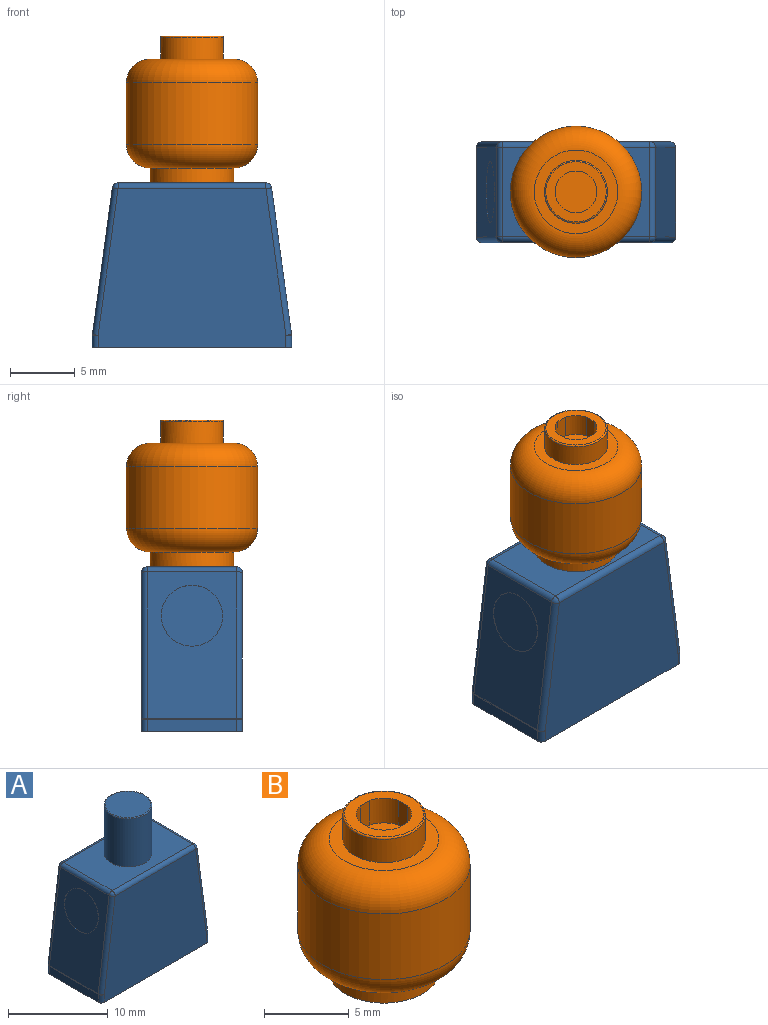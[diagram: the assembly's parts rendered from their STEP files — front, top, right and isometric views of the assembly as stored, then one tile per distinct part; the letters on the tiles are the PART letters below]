
ASSEMBLY  parts=2 mates=1
PART A: 114 faces, bbox 15.4x7.8x18.8 mm
  f0: plane 4.98x2.09mm, normal (0,0,-1), area 6.8mm2, adj f1,f4,f8,f81,f95,f112
  f1: cylinder r=1.5mm len=17.75mm, axis (0,0,-1), area 20.6mm2, adj f0,f16,f81,f82,f105,f112,f113
  f2: cylinder r=1mm len=11.88mm, axis (0,0,-1), area 12.4mm2, adj f10,f80,f87,f105
  f3: cylinder r=1mm len=11.88mm, axis (0,0,-1), area 12.4mm2, adj f11,f88,f89,f96
  f4: cylinder r=1.5mm len=17.75mm, axis (0,0,-1), area 20.6mm2, adj f0,f16,f94,f95,f96,f112,f113
  f5: plane 11.88x0.48mm, normal (0,-1,0), area 5.7mm2, adj f11,f16,f64,f88
  f6: plane 11.88x0.48mm, normal (0,1,0), area 5.7mm2, adj f11,f16,f73,f91
  f7: plane 4.98x2.09mm, normal (0,0,-1), area 6.8mm2, adj f9,f83,f84,f92,f93,f111
  f8: plane 11.88x4.98mm, normal (0,-1,0), area 59.2mm2, adj f0,f16,f81,f95
  f9: plane 11.88x4.98mm, normal (0,1,0), area 59.2mm2, adj f7,f16,f84,f92
  f10: plane 6.06x3.84mm, normal (0,0,-1), area 18.7mm2, adj f2,f13,f15,f26,f27,f29,f52,f53
  f11: plane 6.06x3.84mm, normal (0,0,-1), area 18.7mm2, adj f3,f5,f6,f12,f14,f28,f55,f56
  f12: plane 11.88x2.58mm, normal (0,-1,0), area 22.5mm2, adj f11,f16,f24,f28,f65
  f13: plane 11.88x0.48mm, normal (0,-1,0), area 5.7mm2, adj f10,f16,f69,f80
  f14: plane 11.88x2.58mm, normal (0,1,0), area 22.5mm2, adj f11,f16,f24,f28,f72
  f15: plane 11.88x0.48mm, normal (0,1,0), area 5.7mm2, adj f10,f16,f78,f85
  f16: plane 15.4x7.8mm, normal (0,0,-1), area 42.5mm2, adj f1,f4,f5,f6,f8,f9,f12,f13
  f17: plane 6.92x0.97mm, normal (1,0,0), area 6.7mm2, adj f16,f30,f32,f33
  f18: plane 6.92x0.97mm, normal (-1,0,0), area 6.7mm2, adj f16,f37,f45,f46
  f19: plane 14.52x12.31mm, normal (0,-1,0), area 161.2mm2, adj f16,f30,f34,f37,f40,f41
  f20: plane 11.43x6.92mm, normal (0,0,1), area 61mm2, adj f39,f40,f47,f48,f108
  f21: plane 14.52x12.31mm, normal (0,1,0), area 161.2mm2, adj f16,f32,f38,f46,f47,f51
  f22: plane 11.34x6.92mm, normal (0.99,0,0.13), area 79.2mm2, adj f33,f34,f38,f39
  f23: plane 11.34x6.92mm, normal (-0.99,0,0.13), area 61.5mm2, adj f41,f45,f48,f51,f106
  f24: plane 6.06x0.94mm, normal (-1,0,0), area 5.7mm2, adj f12,f14,f16,f28
  f25: plane 6.06x0.94mm, normal (1,0,0), area 5.7mm2, adj f16,f26,f27,f29
  f26: plane 11.88x2.58mm, normal (0,1,0), area 22.5mm2, adj f10,f16,f25,f29,f76
  f27: plane 11.88x2.58mm, normal (0,-1,0), area 22.5mm2, adj f10,f16,f25,f29,f68
  f28: plane 10.94x6.06mm, normal (-0.99,0,-0.13), area 66.9mm2, adj f11,f12,f14,f24
  f29: plane 10.94x6.06mm, normal (0.99,0,-0.13), area 66.9mm2, adj f10,f25,f26,f27
  f30: cylinder r=0.44mm len=0.97mm, axis (0,0,-1), area 0.7mm2, adj f16,f17,f19,f31
  f31: sphere r=0.44mm, area 0mm2, adj f30,f33,f34
  f32: cylinder r=0.44mm len=0.97mm, axis (0,0,1), area 0.7mm2, adj f16,f17,f21,f35
  f33: cylinder r=0.44mm len=6.92mm, axis (0,-1,0), area 0.4mm2, adj f17,f22,f31,f35
  f34: cylinder r=0.44mm len=11.4mm, axis (-0.13,0,0.99), area 7.9mm2, adj f19,f22,f31,f36
  f35: sphere r=0.44mm, area 0mm2, adj f32,f33,f38
  f36: sphere r=0.44mm, area 0.3mm2, adj f34,f39,f40
  f37: cylinder r=0.44mm len=0.97mm, axis (0,0,1), area 0.7mm2, adj f16,f18,f19,f42
  f38: cylinder r=0.44mm len=11.4mm, axis (0.13,0,-0.99), area 7.9mm2, adj f21,f22,f35,f43
  f39: cylinder r=0.44mm len=6.92mm, axis (0,-1,0), area 4.4mm2, adj f20,f22,f36,f43
  f40: cylinder r=0.44mm len=11.43mm, axis (-1,0,0), area 7.9mm2, adj f19,f20,f36,f44
  f41: cylinder r=0.44mm len=11.4mm, axis (-0.13,0,-0.99), area 7.9mm2, adj f19,f23,f42,f44
  f42: sphere r=0.44mm, area 0mm2, adj f37,f41,f45
  f43: sphere r=0.44mm, area 0.3mm2, adj f38,f39,f47
  f44: sphere r=0.44mm, area 0.3mm2, adj f40,f41,f48
  f45: cylinder r=0.44mm len=6.92mm, axis (0,-1,0), area 0.4mm2, adj f18,f23,f42,f49
  f46: cylinder r=0.44mm len=0.97mm, axis (0,0,-1), area 0.7mm2, adj f16,f18,f21,f49
  f47: cylinder r=0.44mm len=11.43mm, axis (1,0,0), area 7.9mm2, adj f20,f21,f43,f50
  f48: cylinder r=0.44mm len=6.92mm, axis (0,1,0), area 4.4mm2, adj f20,f23,f44,f50
  f49: sphere r=0.44mm, area 0mm2, adj f45,f46,f51
  f50: sphere r=0.44mm, area 0.3mm2, adj f47,f48,f51
  f51: cylinder r=0.44mm len=11.4mm, axis (0.13,0,0.99), area 7.9mm2, adj f21,f23,f49,f50
  f52: plane 11.88x0.4mm, normal (-1,0,0), area 4.8mm2, adj f10,f16,f76,f77
  f53: plane 11.88x0.58mm, normal (0,1,0), area 6.9mm2, adj f10,f16,f77,f79
  f54: plane 11.88x0.4mm, normal (1,0,0), area 4.8mm2, adj f10,f16,f78,f79
  f55: plane 11.88x0.4mm, normal (1,0,0), area 4.8mm2, adj f11,f16,f72,f74
  f56: plane 11.88x0.4mm, normal (-1,0,0), area 4.8mm2, adj f11,f16,f73,f75
  f57: plane 11.88x0.58mm, normal (0,1,0), area 6.9mm2, adj f11,f16,f74,f75
  f58: plane 11.88x0.4mm, normal (-1,0,0), area 4.8mm2, adj f10,f16,f68,f70
  f59: plane 11.88x0.4mm, normal (1,0,0), area 4.8mm2, adj f10,f16,f69,f71
  f60: plane 11.88x0.58mm, normal (0,-1,0), area 6.9mm2, adj f10,f16,f70,f71
  f61: plane 11.88x0.4mm, normal (-1,0,0), area 4.8mm2, adj f11,f16,f64,f66
  f62: plane 11.88x0.4mm, normal (1,0,0), area 4.8mm2, adj f11,f16,f65,f67
  f63: plane 11.88x0.58mm, normal (0,-1,0), area 6.9mm2, adj f11,f16,f66,f67
  f64: cylinder r=0.05mm len=11.88mm, axis (0,0,-1), area 0.9mm2, adj f5,f11,f16,f61
  f65: cylinder r=0.05mm len=11.88mm, axis (0,0,1), area 0.9mm2, adj f11,f12,f16,f62
  f66: cylinder r=0.05mm len=11.88mm, axis (0,0,1), area 0.9mm2, adj f11,f16,f61,f63
  f67: cylinder r=0.05mm len=11.88mm, axis (0,0,-1), area 0.9mm2, adj f11,f16,f62,f63
  f68: cylinder r=0.05mm len=11.88mm, axis (0,0,-1), area 0.9mm2, adj f10,f16,f27,f58
  f69: cylinder r=0.05mm len=11.88mm, axis (0,0,1), area 0.9mm2, adj f10,f13,f16,f59
  f70: cylinder r=0.05mm len=11.88mm, axis (0,0,-1), area 0.9mm2, adj f10,f16,f58,f60
  f71: cylinder r=0.05mm len=11.88mm, axis (0,0,1), area 0.9mm2, adj f10,f16,f59,f60
  f72: cylinder r=0.05mm len=11.88mm, axis (0,0,1), area 0.9mm2, adj f11,f14,f16,f55
  f73: cylinder r=0.05mm len=11.88mm, axis (0,0,-1), area 0.9mm2, adj f6,f11,f16,f56
  f74: cylinder r=0.05mm len=11.88mm, axis (0,0,-1), area 0.9mm2, adj f11,f16,f55,f57
  f75: cylinder r=0.05mm len=11.88mm, axis (0,0,1), area 0.9mm2, adj f11,f16,f56,f57
  f76: cylinder r=0.05mm len=11.88mm, axis (0,0,-1), area 0.9mm2, adj f10,f16,f26,f52
  f77: cylinder r=0.05mm len=11.88mm, axis (0,0,-1), area 0.9mm2, adj f10,f16,f52,f53
  f78: cylinder r=0.05mm len=11.88mm, axis (0,0,1), area 0.9mm2, adj f10,f15,f16,f54
  f79: cylinder r=0.05mm len=11.88mm, axis (0,0,1), area 0.9mm2, adj f10,f16,f53,f54
  f80: cylinder r=1.95mm len=11.88mm, axis (0,0,-1), area 22.5mm2, adj f2,f10,f13,f16
  f81: cylinder r=1.45mm len=11.88mm, axis (0,0,-1), area 16.2mm2, adj f0,f1,f8,f16
  f82: plane 17.24x1.26mm, normal (1,0,0), area 16.8mm2, adj f1,f83,f101,f102,f103,f104,f105,f113
  f83: cylinder r=1.5mm len=17.75mm, axis (0,0,-1), area 20.6mm2, adj f7,f16,f82,f84,f101,f111,f113
  f84: cylinder r=1.45mm len=11.88mm, axis (0,0,-1), area 16.2mm2, adj f7,f9,f16,f83
  f85: cylinder r=1.95mm len=11.88mm, axis (0,0,-1), area 22.5mm2, adj f10,f15,f16,f86
  f86: cylinder r=1mm len=11.88mm, axis (0,0,-1), area 12.4mm2, adj f10,f85,f87,f101
  f87: plane 11.37x1.26mm, normal (-1,0,0), area 9.4mm2, adj f2,f10,f86,f101,f102,f103,f104,f105
  f88: cylinder r=1.95mm len=11.88mm, axis (0,0,-1), area 22.5mm2, adj f3,f5,f11,f16
  f89: plane 11.37x1.26mm, normal (1,0,0), area 9.4mm2, adj f3,f11,f90,f96,f97,f98,f99,f100
  f90: cylinder r=1mm len=11.88mm, axis (0,0,-1), area 12.4mm2, adj f11,f89,f91,f100
  f91: cylinder r=1.95mm len=11.88mm, axis (0,0,-1), area 22.5mm2, adj f6,f11,f16,f90
  f92: cylinder r=1.45mm len=11.88mm, axis (0,0,-1), area 16.2mm2, adj f7,f9,f16,f93
  f93: cylinder r=1.5mm len=17.75mm, axis (0,0,-1), area 20.6mm2, adj f7,f16,f92,f94,f100,f111,f113
  f94: plane 17.24x1.26mm, normal (-1,0,0), area 16.8mm2, adj f4,f93,f96,f97,f98,f99,f100,f113
  f95: cylinder r=1.45mm len=11.88mm, axis (0,0,-1), area 16.2mm2, adj f0,f4,f8,f16
  f96: cylinder r=1mm len=1.01mm, axis (-1,0,0), area 0.8mm2, adj f3,f4,f16,f89,f94,f97
  f97: plane 4x0.5mm, normal (0,-1,0), area 2mm2, adj f89,f94,f96,f98
  f98: cylinder r=0.5mm len=1mm, axis (-1,0,0), area 0.8mm2, adj f89,f94,f97,f99
  f99: plane 4x0.5mm, normal (0,1,0), area 2mm2, adj f89,f94,f98,f100
  f100: cylinder r=1mm len=1.01mm, axis (-1,0,0), area 0.8mm2, adj f16,f89,f90,f93,f94,f99
  f101: cylinder r=1mm len=1.01mm, axis (-1,0,0), area 0.8mm2, adj f16,f82,f83,f86,f87,f102
  f102: plane 4x0.5mm, normal (0,1,0), area 2mm2, adj f82,f87,f101,f103
  f103: cylinder r=0.5mm len=1mm, axis (-1,0,0), area 0.8mm2, adj f82,f87,f102,f104
  f104: plane 4x0.5mm, normal (0,-1,0), area 2mm2, adj f82,f87,f103,f105
  f105: cylinder r=1mm len=1.01mm, axis (-1,0,0), area 0.8mm2, adj f1,f2,f16,f82,f87,f104
  f106: cylinder r=2.38mm len=4.75mm, axis (-0.99,0,0.13), area 0.1mm2, adj f23,f107
  f107: plane 4.75x4.71mm, normal (-0.99,0,0.13), area 17.7mm2, adj f106
  f108: cylinder r=2.4mm len=5.9mm, axis (0,0,-1), area 89mm2, adj f20,f110
  f109: plane 4.6x4.6mm, normal (0,0,1), area 16.6mm2, adj f110
  f110: torus R=2.3mm, axis (0,0,1), area 2.3mm2, adj f108,f109
  f111: cylinder r=1.4mm len=5.87mm, axis (0,0,1), area 13.6mm2, adj f7,f83,f93,f113
  f112: cylinder r=1.4mm len=5.87mm, axis (0,0,1), area 13.6mm2, adj f0,f1,f4,f113
  f113: plane 2.8x2.07mm, normal (0,0,-1), area 5.1mm2, adj f1,f4,f82,f83,f93,f94,f111,f112
PART B: 27 faces, bbox 11x11x11.3 mm
  f0: cylinder r=5.07mm len=10.15mm, axis (0,0,-1), area 150.9mm2, adj f12,f13
  f1: plane 6.47x6.47mm, normal (0,0,1), area 14.3mm2, adj f13,f22
  f2: cylinder r=2.5mm len=8.32mm, axis (0,0,-1), area 20.9mm2, adj f3,f9,f11,f25
  f3: plane 8.32x1.4mm, normal (0,-1,0), area 11.6mm2, adj f2,f4,f11,f25
  f4: cylinder r=2.5mm len=8.32mm, axis (0,0,-1), area 20.9mm2, adj f3,f5,f11,f25
  f5: plane 8.32x1.4mm, normal (-1,0,0), area 11.6mm2, adj f4,f6,f11,f25
  f6: cylinder r=2.5mm len=8.32mm, axis (0,0,-1), area 20.9mm2, adj f5,f7,f11,f25
  f7: plane 8.32x1.4mm, normal (0,1,0), area 11.6mm2, adj f6,f8,f11,f25
  f8: cylinder r=2.5mm len=8.32mm, axis (0,0,-1), area 20.9mm2, adj f7,f9,f11,f25
  f9: plane 8.32x1.4mm, normal (1,0,0), area 11.6mm2, adj f2,f8,f11,f25
  f10: cylinder r=3.23mm len=6.47mm, axis (0,0,-1), area 23.4mm2, adj f11,f12
  f11: plane 6.47x6.47mm, normal (0,0,-1), area 13.6mm2, adj f2,f3,f4,f5,f6,f7,f8,f9
  f12: torus R=3.23mm, axis (0,0,-1), area 80mm2, adj f0,f10
  f13: torus R=3.23mm, axis (0,0,-1), area 80mm2, adj f0,f1
  f14: cylinder r=1.62mm len=1.78mm, axis (0,0,-1), area 3.1mm2, adj f15,f21,f23,f24
  f15: plane 1.78x0.8mm, normal (1,0,0), area 1.4mm2, adj f14,f16,f23,f24
  f16: cylinder r=1.62mm len=1.78mm, axis (0,0,-1), area 3.1mm2, adj f15,f17,f23,f24
  f17: plane 1.78x0.8mm, normal (0,-1,0), area 1.4mm2, adj f16,f18,f23,f24
  f18: cylinder r=1.62mm len=1.78mm, axis (0,0,-1), area 3.1mm2, adj f17,f19,f23,f24
  f19: plane 1.78x0.8mm, normal (-1,0,0), area 1.4mm2, adj f18,f20,f23,f24
  f20: cylinder r=1.62mm len=1.78mm, axis (0,0,-1), area 3.1mm2, adj f19,f21,f23,f24
  f21: plane 1.78x0.8mm, normal (0,1,0), area 1.4mm2, adj f14,f20,f23,f24
  f22: cylinder r=2.43mm len=4.86mm, axis (0,0,-1), area 25.7mm2, adj f1,f26
  f23: plane 4.66x4.66mm, normal (0,0,1), area 8.9mm2, adj f14,f15,f16,f17,f18,f19,f20,f21
  f24: plane 3.15x3.15mm, normal (0,0,1), area 8.2mm2, adj f14,f15,f16,f17,f18,f19,f20,f21
  f25: plane 4.8x4.8mm, normal (0,0,-1), area 19.3mm2, adj f2,f3,f4,f5,f6,f7,f8,f9
  f26: torus R=2.33mm, axis (0,0,1), area 2.4mm2, adj f22,f23
PLACE A t=(-10.94,0.57,-4.14)mm fixed
PLACE B rot(axis=(0,0,1),90deg) t=(-10.94,0.57,8.61)mm
MATE slider B.f2 <-> A.f108  axis (0,0,-1) through (-10.94,0.57,8.61)mm
